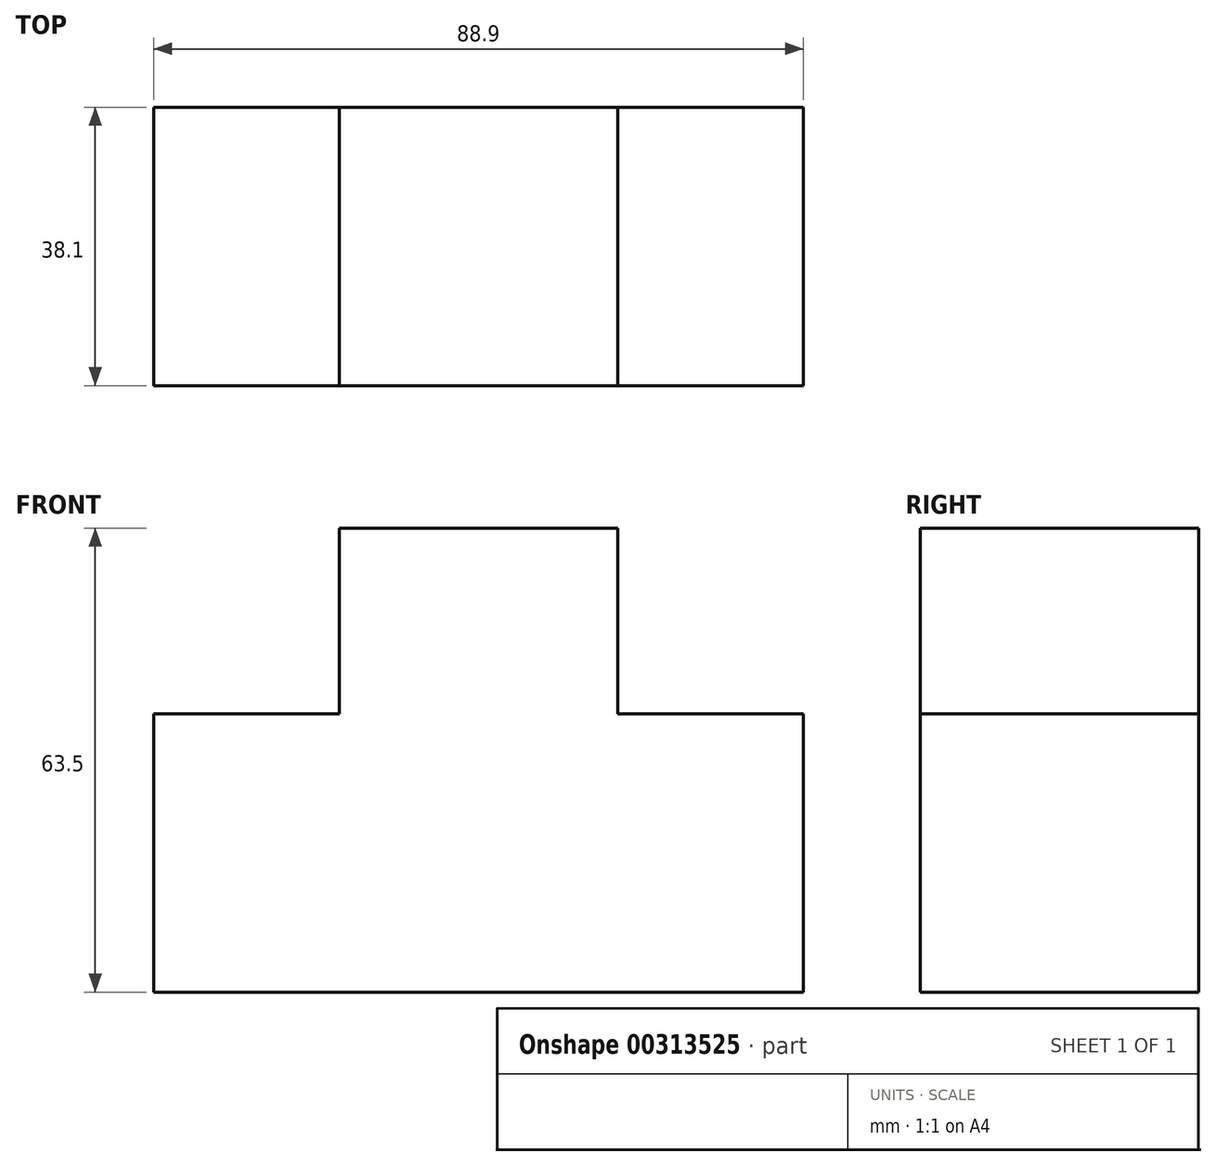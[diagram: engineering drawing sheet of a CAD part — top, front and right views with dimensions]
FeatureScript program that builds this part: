
annotation { "Feature Type Name" : "Feature", "Feature Type Description" : "" }
export const myFeature = defineFeature(function(context is Context, id is Id, definition is map)
    precondition{}
    {
        {
            var Q0;
            Q0=qCreatedBy(makeId("Front.planeOp"),FACE);
            var sketch = newSketch(context, id + "F0", { "sketchPlane" : qUnion([Q0])});
            skLineSegment(sketch, "E0", {"start": v(-52.94, -50.7) * mm, "end": v(35.96, -50.7) * mm});
            skLineSegment(sketch, "E1", {"start": v(35.96, -50.7) * mm, "end": v(35.96, -12.6) * mm});
            skLineSegment(sketch, "E2", {"start": v(35.96, -12.6) * mm, "end": v(10.56, -12.6) * mm});
            skLineSegment(sketch, "E3", {"start": v(10.56, -12.6) * mm, "end": v(10.56, 12.8) * mm});
            skLineSegment(sketch, "E4", {"start": v(10.56, 12.8) * mm, "end": v(-27.54, 12.8) * mm});
            skLineSegment(sketch, "E5", {"start": v(-27.54, 12.8) * mm, "end": v(-27.54, -12.6) * mm});
            skLineSegment(sketch, "E6", {"start": v(-27.54, -12.6) * mm, "end": v(-52.94, -12.6) * mm});
            skLineSegment(sketch, "E7", {"start": v(-52.94, -12.6) * mm, "end": v(-52.94, -50.7) * mm});
            skSolve(sketch);
        }
        {
            var Q0;
            Q0=makeQuery(id+"F0.imprint","IMPRINT",FACE,{"disambiguationData":[TD([[makeQuery(id+"F0.imprint","IMPRINT",EDGE,{"derivedFrom":sQuery(id+"F0.wireOp",EDGE,"E0")}),1.0]])]});
            extrude(context, id + "F1", {"entities" : qUnion([Q0]), "depth" : 38.1 * mm});
        }
    });
